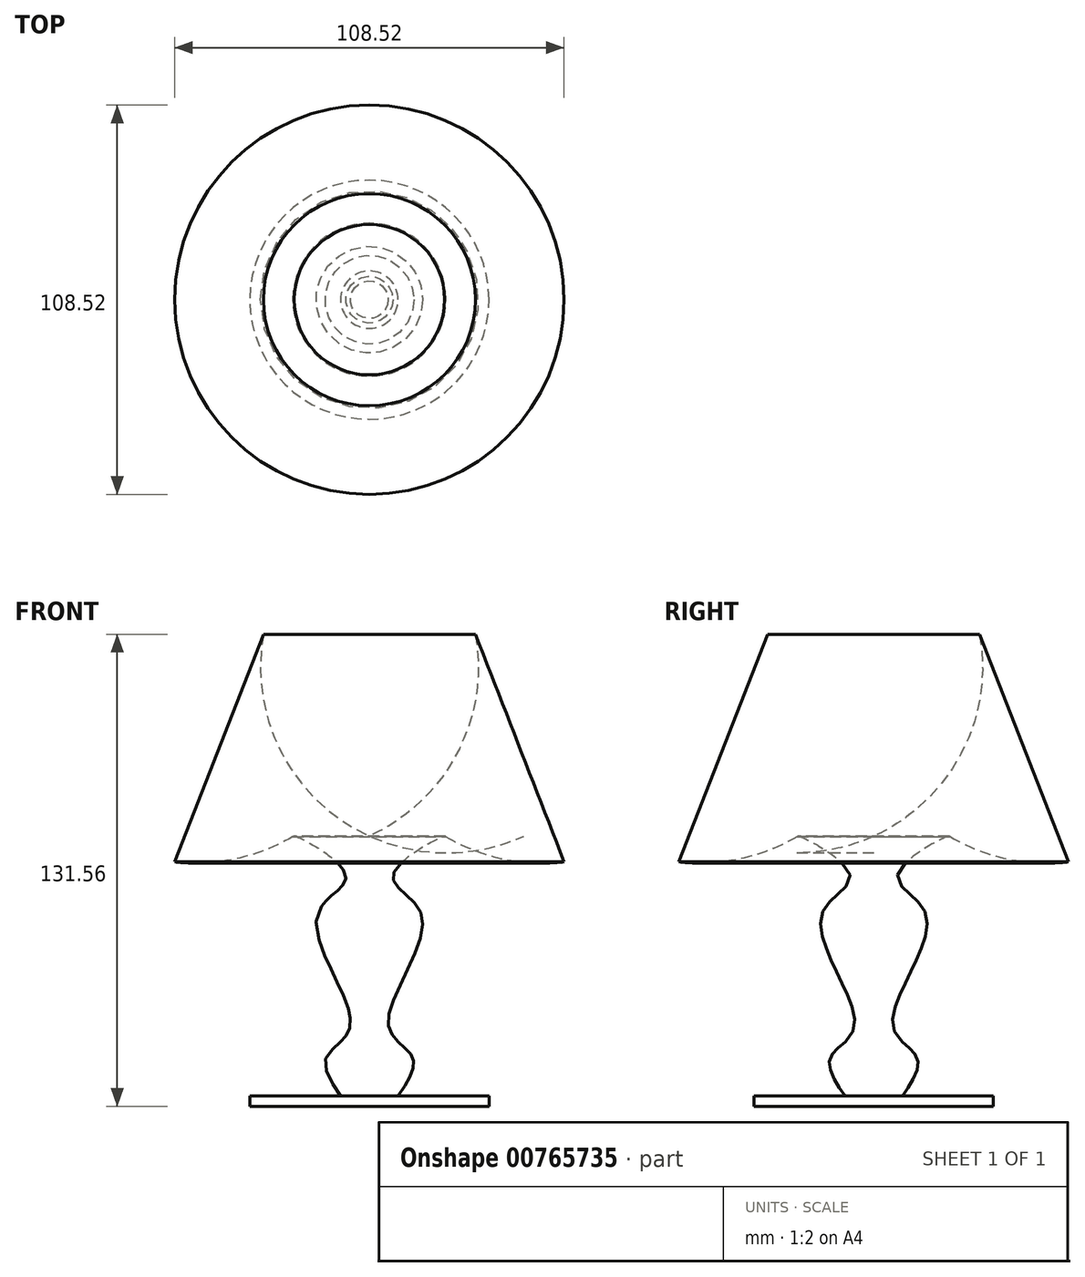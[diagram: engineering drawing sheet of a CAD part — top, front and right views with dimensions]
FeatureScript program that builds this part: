
annotation { "Feature Type Name" : "Feature", "Feature Type Description" : "" }
export const myFeature = defineFeature(function(context is Context, id is Id, definition is map)
    precondition{}
    {
        {
            var Q0;
            Q0=qCreatedBy(makeId("Front.planeOp"),FACE);
            var sketch = newSketch(context, id + "F0", { "sketchPlane" : qUnion([Q0])});
            skLineSegment(sketch, "E0", {"start": v(0, 0) * mm, "end": v(-20.96, 0) * mm, "construction": true});
            skLineSegment(sketch, "E1.bottom", {"start": v(-20.96, 0) * mm, "end": v(-54.28, 0) * mm});
            skLineSegment(sketch, "E1.top", {"start": v(-20.96, 2.87) * mm, "end": v(-54.28, 2.87) * mm});
            skLineSegment(sketch, "E1.left", {"start": v(-20.96, 0) * mm, "end": v(-20.96, 2.87) * mm});
            skLineSegment(sketch, "E1.right", {"start": v(-54.28, 0) * mm, "end": v(-54.28, 2.87) * mm});
            skFitSpline(sketch, "E2", {"points": [v(-28.98, 2.87) * mm, v(-32.93, 13.82) * mm, v(-26.22, 22.82) * mm, v(-35.6, 53.11) * mm, v(-27.6, 64.66) * mm, v(-42.24, 75.3) * mm, v(-42.24, 75.1) * mm, v(-42.04, 75.3) * mm], "startDerivative": vector(-57.17, 83.29) * mm, "endDerivative": vector(8.81, 14.05) * mm});
            skLineSegment(sketch, "E3", {"start": v(-42.04, 75.3) * mm, "end": v(-20.96, 75.3) * mm});
            skLineSegment(sketch, "E4", {"start": v(-20.96, 75.3) * mm, "end": v(-20.96, 2.87) * mm});
            skArc(sketch, "E5", {"start": v(-75.22, 68.12) * mm, "mid": v(-58.04, 68.98) * mm, "end": v(-42.04, 75.3) * mm});
            skLineSegment(sketch, "E6", {"start": v(-75.22, 68.12) * mm, "end": v(-50.52, 131.56) * mm});
            skArc(sketch, "E7", {"start": v(-50.52, 131.56) * mm, "mid": v(-45.37, 98.37) * mm, "end": v(-20.96, 75.3) * mm});
            skSolve(sketch);
        }
        {
            var Q0;
            Q0 = qSketchRegion(id + "F0", true);
            var Q1;
            Q1=sQuery(id+"F0.wireOp",EDGE,"E4");
            revolve(context, id + "F1", {"surfaceOperationType" : NewSurfaceOperationType.NEW, "entities" : qUnion([Q0]), "axis" : qUnion([Q1]), "revolveType" : RevolveType.FULL});
        }
    });
